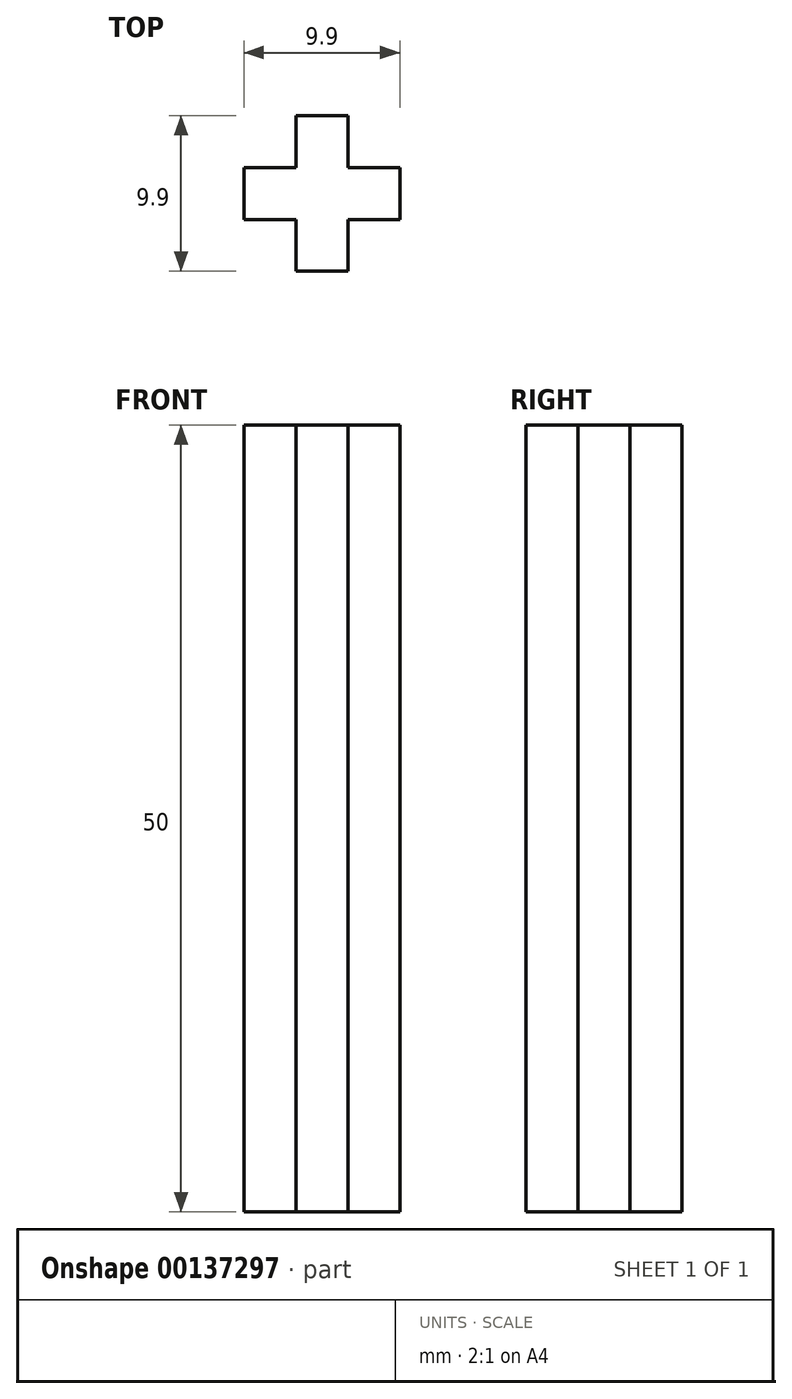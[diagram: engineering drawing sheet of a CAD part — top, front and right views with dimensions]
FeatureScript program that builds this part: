
annotation { "Feature Type Name" : "Feature", "Feature Type Description" : "" }
export const myFeature = defineFeature(function(context is Context, id is Id, definition is map)
    precondition{}
    {
        {
            var Q0;
            Q0=qCreatedBy(makeId("Top.planeOp"),FACE);
            var sketch = newSketch(context, id + "F0", { "sketchPlane" : qUnion([Q0])});
            skLineSegment(sketch, "E0.bottom", {"start": v(4.95, -1.65) * mm, "end": v(1.65, -1.65) * mm});
            skLineSegment(sketch, "E0.top", {"start": v(4.95, 1.65) * mm, "end": v(1.65, 1.65) * mm});
            skLineSegment(sketch, "E0.left", {"start": v(4.95, -1.65) * mm, "end": v(4.95, 1.65) * mm});
            skLineSegment(sketch, "E0.right", {"start": v(-4.95, -1.65) * mm, "end": v(-4.95, 1.65) * mm});
            skPoint(sketch, "E0.middle", {"position": v(0, 0) * mm});
            skLineSegment(sketch, "E1.bottom", {"start": v(1.65, 4.95) * mm, "end": v(-1.65, 4.95) * mm});
            skLineSegment(sketch, "E1.top", {"start": v(1.65, -4.95) * mm, "end": v(-1.65, -4.95) * mm});
            skLineSegment(sketch, "E1.left", {"start": v(1.65, 4.95) * mm, "end": v(1.65, 1.65) * mm});
            skLineSegment(sketch, "E1.right", {"start": v(-1.65, 4.95) * mm, "end": v(-1.65, 1.65) * mm});
            skLineSegment(sketch, "E2.trimOffspring", {"start": v(-1.65, -1.65) * mm, "end": v(-1.65, -4.95) * mm});
            skLineSegment(sketch, "E3.trimOffspring", {"start": v(-1.65, 1.65) * mm, "end": v(-4.95, 1.65) * mm});
            skLineSegment(sketch, "E4.trimOffspring", {"start": v(1.65, -1.65) * mm, "end": v(1.65, -4.95) * mm});
            skLineSegment(sketch, "E5.trimOffspring", {"start": v(-1.65, -1.65) * mm, "end": v(-4.95, -1.65) * mm});
            skSolve(sketch);
        }
        {
            var Q0;
            Q0=makeQuery(id+"F0.imprint","IMPRINT",FACE,{"disambiguationData":[TD([[makeQuery(id+"F0.imprint","IMPRINT",EDGE,{"derivedFrom":sQuery(id+"F0.wireOp",EDGE,"E0.bottom")}),-1.0]])]});
            extrude(context, id + "F1", {"entities" : qUnion([Q0]), "depth" : 50 * mm});
        }
    });
